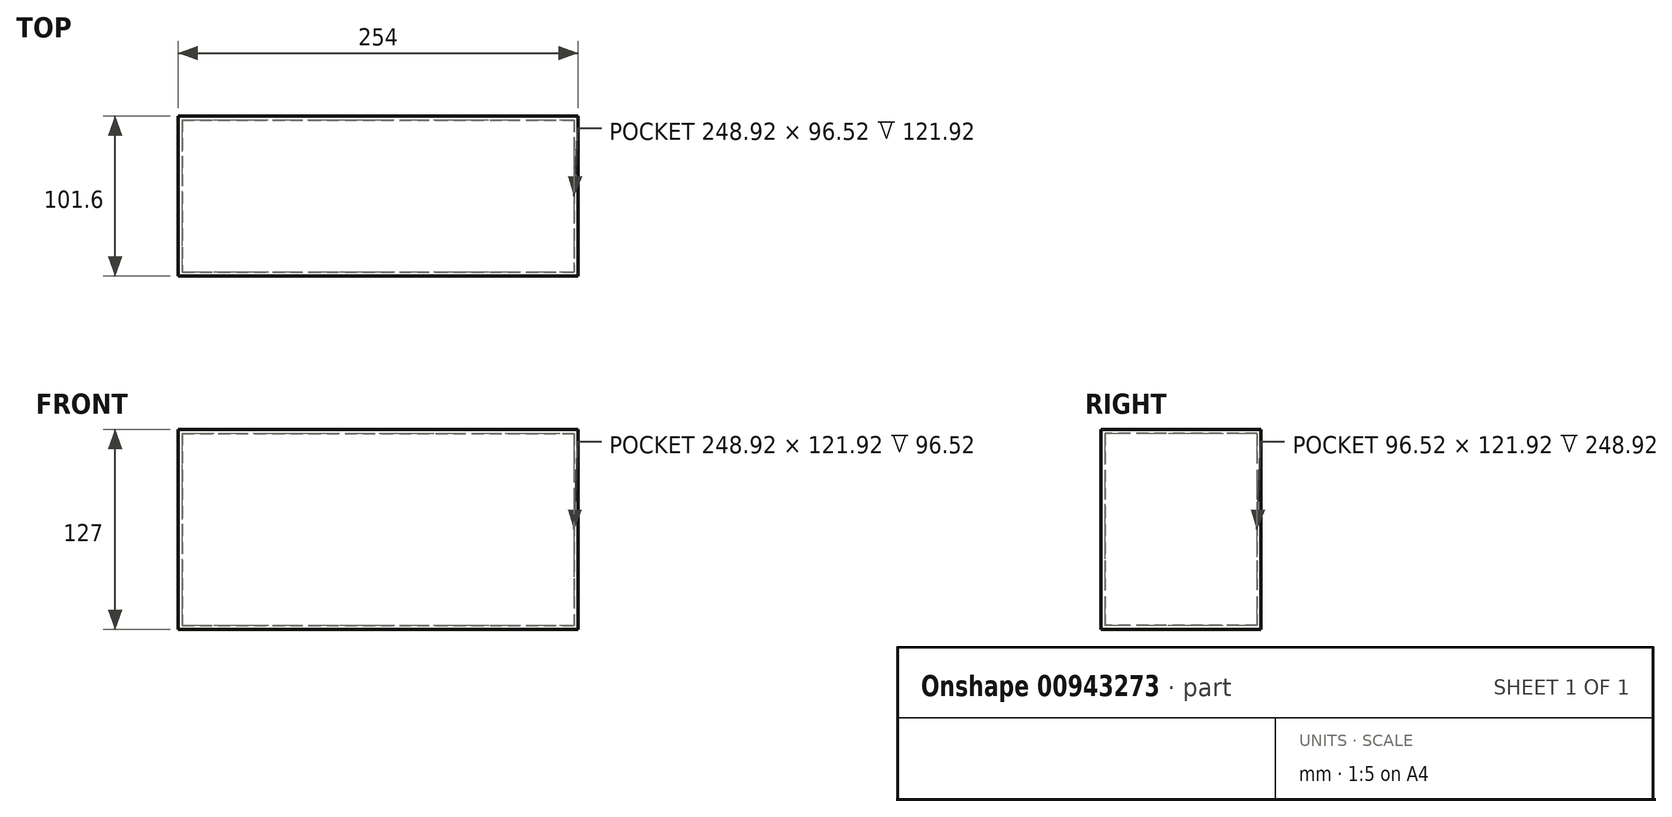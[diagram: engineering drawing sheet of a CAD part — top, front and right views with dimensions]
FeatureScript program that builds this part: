
annotation { "Feature Type Name" : "Feature", "Feature Type Description" : "" }
export const myFeature = defineFeature(function(context is Context, id is Id, definition is map)
    precondition{}
    {
        {
            var Q0;
            Q0=qCreatedBy(makeId("Front.planeOp"),FACE);
            var sketch = newSketch(context, id + "F0", { "sketchPlane" : qUnion([Q0])});
            skLineSegment(sketch, "E0.bottom", {"start": v(-127, 63.5) * mm, "end": v(127, 63.5) * mm});
            skLineSegment(sketch, "E0.top", {"start": v(-127, -63.5) * mm, "end": v(127, -63.5) * mm});
            skLineSegment(sketch, "E0.left", {"start": v(-127, 63.5) * mm, "end": v(-127, -63.5) * mm});
            skLineSegment(sketch, "E0.right", {"start": v(127, 63.5) * mm, "end": v(127, -63.5) * mm});
            skPoint(sketch, "E0.middle", {"position": v(0, 0) * mm});
            skSolve(sketch);
        }
        {
            var Q0;
            Q0 = qSketchRegion(id + "F0", true);
            extrude(context, id + "F1", {"entities" : qUnion([Q0]), "oppositeDirection" : true, "depth" : 101.6 * mm, "offsetDistance" : 25.4 * mm});
        }
        {
            var Q0;
            Q0=makeQuery(id+"F1.opExtrude","CAP_FACE",FACE,{"disambiguationData":[OSD([sQuery(id+"F0.wireOp",EDGE,"E0.bottom"),sQuery(id+"F0.wireOp",EDGE,"E0.top"),sQuery(id+"F0.wireOp",EDGE,"E0.left"),sQuery(id+"F0.wireOp",EDGE,"E0.right")])],"isStart":true});
            shell(context, id + "F2", {"entities" : qUnion([Q0]), "thickness" : 2.54 * mm});
        }
        {
            var Q0;
            Q0=makeQuery(id+"F1.opExtrude","CAP_FACE",FACE,{"disambiguationData":[OSD([sQuery(id+"F0.wireOp",EDGE,"E0.bottom"),sQuery(id+"F0.wireOp",EDGE,"E0.top"),sQuery(id+"F0.wireOp",EDGE,"E0.left"),sQuery(id+"F0.wireOp",EDGE,"E0.right")])],"isStart":true});
            var sketch = newSketch(context, id + "F3", { "sketchPlane" : qUnion([Q0])});
            skLineSegment(sketch, "E1.bottom", {"start": v(-124.46, 60.96) * mm, "end": v(124.46, 60.96) * mm});
            skLineSegment(sketch, "E1.top", {"start": v(-124.46, -60.96) * mm, "end": v(124.46, -60.96) * mm});
            skLineSegment(sketch, "E1.left", {"start": v(-124.46, 60.96) * mm, "end": v(-124.46, -60.96) * mm});
            skLineSegment(sketch, "E1.right", {"start": v(124.46, 60.96) * mm, "end": v(124.46, -60.96) * mm});
            skPoint(sketch, "E1.middle", {"position": v(0, 0) * mm});
            skSolve(sketch);
        }
        {
            var Q0;
            Q0 = qSketchRegion(id + "F3", true);
            extrude(context, id + "F4", {"entities" : qUnion([Q0]), "operationType" : NewBodyOperationType.ADD, "oppositeDirection" : true, "depth" : 2.54 * mm, "offsetDistance" : 25.4 * mm});
        }
    });
